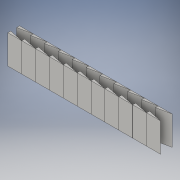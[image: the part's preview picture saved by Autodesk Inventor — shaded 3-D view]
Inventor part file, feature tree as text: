
AUTODESK INVENTOR PART (.ipt)
format: ipt  version: 2016 (Build 200138000, 138)  size: 174,592 bytes
history: native  units: in
note: dims shown in document units (in); Inventor stores cm internally (conversion verified against a paired STEP export)
features: extrude x1, sketch x1
ambient origin geometry x8: Origin, YZ Plane, XZ Plane, XY Plane, X Axis, Y Axis, Z Axis, Center Point
bodies: Body1 (feature_tree)
feature tree (2):
  extrude  "Extrusion2"  Depth=0.074in
  sketch  "Sketch3"  dims[d34=0.0739in d35=0.0158in d36=0.0315in d37=1.182in d38=2.3622in d40=0.148in d41=0.3937in d43=1.0in d45=0.154in d46=0.0in d47=0.7874in d49=0.074in d50=0.3937in d52=1.0in]
